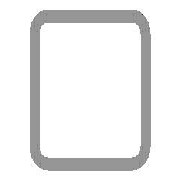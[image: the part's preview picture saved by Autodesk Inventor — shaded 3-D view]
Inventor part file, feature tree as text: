
AUTODESK INVENTOR PART (.ipt)
format: ipt  version: 2018 (Build 220112000, 112)  size: 145,408 bytes
history: native  units: mm (DEFAULTED — no unit token found)
features: other x4, sketch x4, extrude x2, plane x1
ambient origin geometry x8: Origin, YZ Plane, XZ Plane, XY Plane, X Axis, Y Axis, Z Axis, Center Point
bodies: Solid1 (feature_tree)
feature tree (11):
  other  "Piantone tubolare l min"
  other  "Driven Length"
  other  "Piano iniziale"
  other  "Piano finale"
  extrude  "Corpo"  TaperAngle=0.0deg  [1 undecoded]
  extrude  "Estrusione2"  Depth=40.0mm
  sketch  "Schizzo"
  sketch  "Sketch3"  dims[d3=685.5mm d4=0.0mm]
  plane  "Work Plane3"
  sketch  "Sketch4"  dims[d7=4.0mm d9=40.0mm d11=40.0mm d12=2.0mm d13=-0.0mm d14=685.5mm d15=20.0mm d16=20.0mm d17=90.0deg d18=685.5mm d19=45.0deg d20=10.0mm d21=0.0mm]
  sketch  "Schizzo5"
note: 1 required parameter value undecoded (feature->parameter linkage not recoverable at this tier; creation-order binding heuristic only, values carry confidence <= 0.55)
